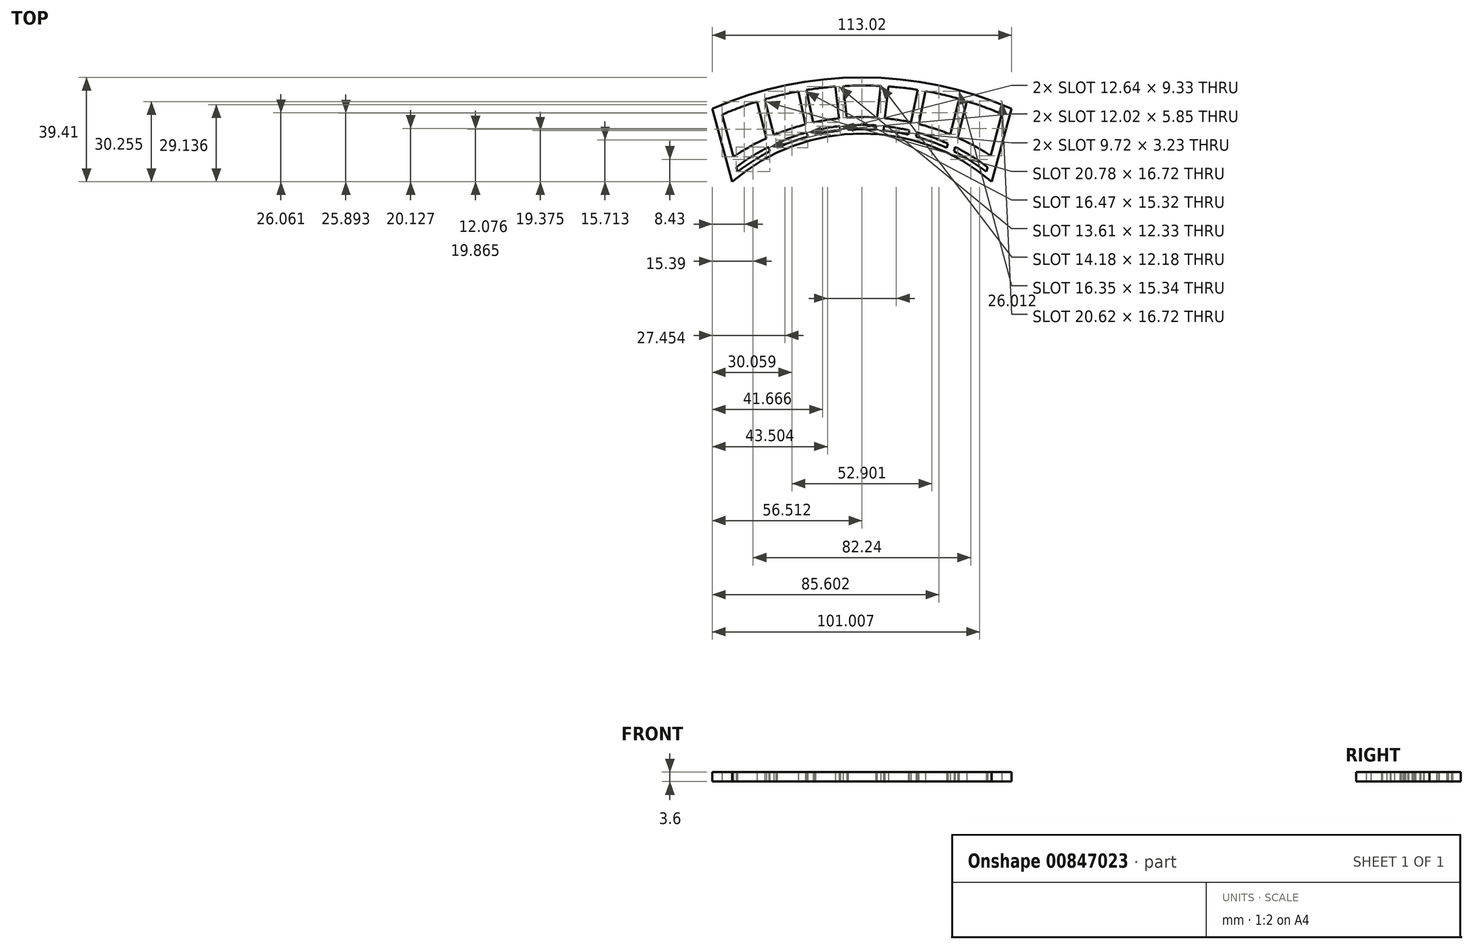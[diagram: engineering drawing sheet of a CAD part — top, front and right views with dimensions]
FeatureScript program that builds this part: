
annotation { "Feature Type Name" : "Feature", "Feature Type Description" : "" }
export const myFeature = defineFeature(function(context is Context, id is Id, definition is map)
    precondition{}
    {
        {
            var Q0;
            Q0=qCreatedBy(makeId("Top.planeOp"),FACE);
            var sketch = newSketch(context, id + "F0", { "sketchPlane" : qUnion([Q0])});
            skArc(sketch, "E0", {"start": v(50, 0) * mm, "mid": v(0, 17.98) * mm, "end": v(-50, 0) * mm});
            skLineSegment(sketch, "E1", {"start": v(-49.07, -3.46) * mm, "end": v(-56.5, 24.14) * mm});
            skLineSegment(sketch, "E2.MirrorCS", {"start": v(49.07, -3.46) * mm, "end": v(56.5, 24.14) * mm});
            skPoint(sketch, "E3", {"position": v(0, 35.95) * mm});
            skPoint(sketch, "E3.positionSnap0", {"position": v(0, 17.98) * mm});
            skArc(sketch, "E4", {"start": v(56.5, 24.14) * mm, "mid": v(0, 35.95) * mm, "end": v(-56.5, 24.14) * mm});
            skLineSegment(sketch, "E5", {"start": v(-53.72, 25.32) * mm, "end": v(-46.52, -1.37) * mm});
            skLineSegment(sketch, "E6", {"start": v(-40.42, 30.04) * mm, "end": v(-34.4, 6.4) * mm});
            skLineSegment(sketch, "E7", {"start": v(-37.53, 30.87) * mm, "end": v(-31.64, 7.75) * mm});
            skLineSegment(sketch, "E8", {"start": v(-20.12, 11.99) * mm, "end": v(-24.6, 33.79) * mm});
            skLineSegment(sketch, "E9", {"start": v(-17.2, 12.73) * mm, "end": v(-21.65, 34.28) * mm});
            skLineSegment(sketch, "E10", {"start": v(-10.45, 35.56) * mm, "end": v(-7.96, 14.3) * mm});
            skLineSegment(sketch, "E11", {"start": v(-7.45, 35.75) * mm, "end": v(-4.97, 14.56) * mm});
            skLineSegment(sketch, "E12.MirrorCS", {"start": v(7.45, 35.75) * mm, "end": v(4.97, 14.56) * mm});
            skLineSegment(sketch, "E13.MirrorCS", {"start": v(10.45, 35.56) * mm, "end": v(7.96, 14.3) * mm});
            skLineSegment(sketch, "E14.MirrorCS", {"start": v(17.2, 12.73) * mm, "end": v(21.65, 34.28) * mm});
            skLineSegment(sketch, "E15.MirrorCS", {"start": v(20.12, 11.99) * mm, "end": v(24.6, 33.79) * mm});
            skLineSegment(sketch, "E16.MirrorCS", {"start": v(37.53, 30.87) * mm, "end": v(31.64, 7.75) * mm});
            skLineSegment(sketch, "E17.MirrorCS", {"start": v(40.42, 30.04) * mm, "end": v(34.4, 6.4) * mm});
            skLineSegment(sketch, "E18.MirrorCS", {"start": v(53.72, 25.32) * mm, "end": v(46.52, -1.37) * mm});
            skArc(sketch, "E19", {"start": v(55.64, 20.9) * mm, "mid": v(0, 32.89) * mm, "end": v(-55.57, 20.66) * mm});
            skPoint(sketch, "E19.startSnap0", {"position": v(-35, 20.9) * mm});
            skArc(sketch, "E20", {"start": v(51.23, 4.55) * mm, "mid": v(0, 20.9) * mm, "end": v(-51.13, 4.18) * mm});
            skPoint(sketch, "E20.midSnap0", {"position": v(35, 20.9) * mm});
            skPoint(sketch, "E20.midSnap1", {"position": v(0, 32.89) * mm});
            skArc(sketch, "E21.0", {"start": v(49.53, -1.75) * mm, "mid": v(0, 16.33) * mm, "end": v(-49.53, -1.75) * mm});
            skArc(sketch, "E22.0", {"start": v(49.07, -3.46) * mm, "mid": v(0, 14.73) * mm, "end": v(-49.07, -3.46) * mm});
            skPoint(sketch, "E23.orphan", {"position": v(-47.44, 2.03) * mm});
            skPoint(sketch, "E24.orphan", {"position": v(-35.22, 9.64) * mm});
            skPoint(sketch, "E25.orphan", {"position": v(-32.46, 10.95) * mm});
            skPoint(sketch, "E26.orphan", {"position": v(-20.78, 15.18) * mm});
            skPoint(sketch, "E27.orphan", {"position": v(-17.87, 15.92) * mm});
            skPoint(sketch, "E28.orphan", {"position": v(-8.34, 17.53) * mm});
            skPoint(sketch, "E29.orphan", {"position": v(-5.35, 17.8) * mm});
            skPoint(sketch, "E30.orphan", {"position": v(5.35, 17.8) * mm});
            skPoint(sketch, "E31.orphan", {"position": v(8.34, 17.53) * mm});
            skPoint(sketch, "E32.orphan", {"position": v(17.87, 15.92) * mm});
            skPoint(sketch, "E33.orphan", {"position": v(20.78, 15.18) * mm});
            skPoint(sketch, "E34.orphan", {"position": v(32.46, 10.95) * mm});
            skPoint(sketch, "E35.orphan", {"position": v(35.22, 9.64) * mm});
            skPoint(sketch, "E36.orphan", {"position": v(47.44, 2.03) * mm});
            skPoint(sketch, "E37.orphan", {"position": v(50, 0) * mm});
            skSolve(sketch);
        }
        {
            var Q0;
            {var subQ0=sQuery(id+"F0.wireOp",EDGE,"E4");var subQ1=sQuery(id+"F0.wireOp",EDGE,"E1");var subQ2=makeQuery(id+"F0.imprint","INTERSECT",VERTEX,{"derivedFrom":[subQ1,subQ0]});Q0=makeQuery(id+"F0.imprint","IMPRINT",FACE,{"disambiguationData":[TD([[makeQuery(id+"F0.imprint","IMPRINT",EDGE,{"disambiguationData":[TD([[subQ2,1.0]])],"derivedFrom":subQ1}),-1.0]])]});}
            var Q1;
            {var subQ0=sQuery(id+"F0.wireOp",EDGE,"E5");var subQ1=sQuery(id+"F0.wireOp",EDGE,"E4");var subQ2=makeQuery(id+"F0.imprint","INTERSECT",VERTEX,{"derivedFrom":[subQ1,subQ0]});Q1=makeQuery(id+"F0.imprint","IMPRINT",FACE,{"disambiguationData":[TD([[makeQuery(id+"F0.imprint","IMPRINT",EDGE,{"disambiguationData":[TD([[subQ2,1.0]])],"derivedFrom":subQ1}),1.0]])]});}
            var Q2;
            {var subQ0=sQuery(id+"F0.wireOp",EDGE,"E6");var subQ1=sQuery(id+"F0.wireOp",EDGE,"E4");var subQ2=makeQuery(id+"F0.imprint","INTERSECT",VERTEX,{"derivedFrom":[subQ1,subQ0]});Q2=makeQuery(id+"F0.imprint","IMPRINT",FACE,{"disambiguationData":[TD([[makeQuery(id+"F0.imprint","IMPRINT",EDGE,{"disambiguationData":[TD([[subQ2,1.0]])],"derivedFrom":subQ1}),1.0]])]});}
            var Q3;
            {var subQ0=sQuery(id+"F0.wireOp",EDGE,"E7");var subQ1=sQuery(id+"F0.wireOp",EDGE,"E4");var subQ2=makeQuery(id+"F0.imprint","INTERSECT",VERTEX,{"derivedFrom":[subQ1,subQ0]});Q3=makeQuery(id+"F0.imprint","IMPRINT",FACE,{"disambiguationData":[TD([[makeQuery(id+"F0.imprint","IMPRINT",EDGE,{"disambiguationData":[TD([[subQ2,1.0]])],"derivedFrom":subQ1}),1.0]])]});}
            var Q4;
            {var subQ0=sQuery(id+"F0.wireOp",EDGE,"E8");var subQ1=sQuery(id+"F0.wireOp",EDGE,"E4");var subQ2=makeQuery(id+"F0.imprint","INTERSECT",VERTEX,{"derivedFrom":[subQ1,subQ0]});Q4=makeQuery(id+"F0.imprint","IMPRINT",FACE,{"disambiguationData":[TD([[makeQuery(id+"F0.imprint","IMPRINT",EDGE,{"disambiguationData":[TD([[subQ2,1.0]])],"derivedFrom":subQ1}),1.0]])]});}
            var Q5;
            {var subQ0=sQuery(id+"F0.wireOp",EDGE,"E9");var subQ1=sQuery(id+"F0.wireOp",EDGE,"E4");var subQ2=makeQuery(id+"F0.imprint","INTERSECT",VERTEX,{"derivedFrom":[subQ1,subQ0]});Q5=makeQuery(id+"F0.imprint","IMPRINT",FACE,{"disambiguationData":[TD([[makeQuery(id+"F0.imprint","IMPRINT",EDGE,{"disambiguationData":[TD([[subQ2,1.0]])],"derivedFrom":subQ1}),1.0]])]});}
            var Q6;
            {var subQ0=sQuery(id+"F0.wireOp",EDGE,"E10");var subQ1=sQuery(id+"F0.wireOp",EDGE,"E4");var subQ2=makeQuery(id+"F0.imprint","INTERSECT",VERTEX,{"derivedFrom":[subQ1,subQ0]});Q6=makeQuery(id+"F0.imprint","IMPRINT",FACE,{"disambiguationData":[TD([[makeQuery(id+"F0.imprint","IMPRINT",EDGE,{"disambiguationData":[TD([[subQ2,1.0]])],"derivedFrom":subQ1}),1.0]])]});}
            var Q7;
            {var subQ0=sQuery(id+"F0.wireOp",EDGE,"E11");var subQ1=sQuery(id+"F0.wireOp",EDGE,"E4");var subQ2=makeQuery(id+"F0.imprint","INTERSECT",VERTEX,{"derivedFrom":[subQ1,subQ0]});Q7=makeQuery(id+"F0.imprint","IMPRINT",FACE,{"disambiguationData":[TD([[makeQuery(id+"F0.imprint","IMPRINT",EDGE,{"disambiguationData":[TD([[subQ2,1.0]])],"derivedFrom":subQ1}),1.0]])]});}
            var Q8;
            {var subQ0=sQuery(id+"F0.wireOp",EDGE,"E12.MirrorCS");var subQ1=sQuery(id+"F0.wireOp",EDGE,"E4");var subQ2=makeQuery(id+"F0.imprint","INTERSECT",VERTEX,{"derivedFrom":[subQ1,subQ0]});Q8=makeQuery(id+"F0.imprint","IMPRINT",FACE,{"disambiguationData":[TD([[makeQuery(id+"F0.imprint","IMPRINT",EDGE,{"disambiguationData":[TD([[subQ2,1.0]])],"derivedFrom":subQ1}),1.0]])]});}
            var Q9;
            {var subQ0=sQuery(id+"F0.wireOp",EDGE,"E13.MirrorCS");var subQ1=sQuery(id+"F0.wireOp",EDGE,"E4");var subQ2=makeQuery(id+"F0.imprint","INTERSECT",VERTEX,{"derivedFrom":[subQ1,subQ0]});Q9=makeQuery(id+"F0.imprint","IMPRINT",FACE,{"disambiguationData":[TD([[makeQuery(id+"F0.imprint","IMPRINT",EDGE,{"disambiguationData":[TD([[subQ2,1.0]])],"derivedFrom":subQ1}),1.0]])]});}
            var Q10;
            {var subQ0=sQuery(id+"F0.wireOp",EDGE,"E14.MirrorCS");var subQ1=sQuery(id+"F0.wireOp",EDGE,"E4");var subQ2=makeQuery(id+"F0.imprint","INTERSECT",VERTEX,{"derivedFrom":[subQ1,subQ0]});Q10=makeQuery(id+"F0.imprint","IMPRINT",FACE,{"disambiguationData":[TD([[makeQuery(id+"F0.imprint","IMPRINT",EDGE,{"disambiguationData":[TD([[subQ2,1.0]])],"derivedFrom":subQ1}),1.0]])]});}
            var Q11;
            {var subQ0=sQuery(id+"F0.wireOp",EDGE,"E15.MirrorCS");var subQ1=sQuery(id+"F0.wireOp",EDGE,"E4");var subQ2=makeQuery(id+"F0.imprint","INTERSECT",VERTEX,{"derivedFrom":[subQ1,subQ0]});Q11=makeQuery(id+"F0.imprint","IMPRINT",FACE,{"disambiguationData":[TD([[makeQuery(id+"F0.imprint","IMPRINT",EDGE,{"disambiguationData":[TD([[subQ2,1.0]])],"derivedFrom":subQ1}),1.0]])]});}
            var Q12;
            {var subQ0=sQuery(id+"F0.wireOp",EDGE,"E16.MirrorCS");var subQ1=sQuery(id+"F0.wireOp",EDGE,"E4");var subQ2=makeQuery(id+"F0.imprint","INTERSECT",VERTEX,{"derivedFrom":[subQ1,subQ0]});Q12=makeQuery(id+"F0.imprint","IMPRINT",FACE,{"disambiguationData":[TD([[makeQuery(id+"F0.imprint","IMPRINT",EDGE,{"disambiguationData":[TD([[subQ2,1.0]])],"derivedFrom":subQ1}),1.0]])]});}
            var Q13;
            {var subQ0=sQuery(id+"F0.wireOp",EDGE,"E17.MirrorCS");var subQ1=sQuery(id+"F0.wireOp",EDGE,"E4");var subQ2=makeQuery(id+"F0.imprint","INTERSECT",VERTEX,{"derivedFrom":[subQ1,subQ0]});Q13=makeQuery(id+"F0.imprint","IMPRINT",FACE,{"disambiguationData":[TD([[makeQuery(id+"F0.imprint","IMPRINT",EDGE,{"disambiguationData":[TD([[subQ2,1.0]])],"derivedFrom":subQ1}),1.0]])]});}
            var Q14;
            {var subQ0=sQuery(id+"F0.wireOp",EDGE,"E4");var subQ1=sQuery(id+"F0.wireOp",EDGE,"E2.MirrorCS");var subQ2=makeQuery(id+"F0.imprint","INTERSECT",VERTEX,{"derivedFrom":[subQ1,subQ0]});Q14=makeQuery(id+"F0.imprint","IMPRINT",FACE,{"disambiguationData":[TD([[makeQuery(id+"F0.imprint","IMPRINT",EDGE,{"disambiguationData":[TD([[subQ2,1.0]])],"derivedFrom":subQ1}),1.0]])]});}
            var Q15;
            {var subQ0=sQuery(id+"F0.wireOp",EDGE,"E22.0");var subQ1=sQuery(id+"F0.wireOp",EDGE,"E1");var subQ2=makeQuery(id+"F0.imprint","INTERSECT",VERTEX,{"derivedFrom":[subQ1,subQ0]});Q15=makeQuery(id+"F0.imprint","IMPRINT",FACE,{"disambiguationData":[TD([[makeQuery(id+"F0.imprint","IMPRINT",EDGE,{"disambiguationData":[TD([[subQ2,-1.0]])],"derivedFrom":subQ1}),-1.0]])]});}
            var Q16;
            {var subQ0=sQuery(id+"F0.wireOp",EDGE,"E22.0");var subQ1=sQuery(id+"F0.wireOp",EDGE,"E5");var subQ2=makeQuery(id+"F0.imprint","INTERSECT",VERTEX,{"derivedFrom":[subQ1,subQ0]});Q16=makeQuery(id+"F0.imprint","IMPRINT",FACE,{"disambiguationData":[TD([[makeQuery(id+"F0.imprint","IMPRINT",EDGE,{"disambiguationData":[TD([[subQ2,1.0]])],"derivedFrom":subQ1}),1.0]])]});}
            var Q17;
            {var subQ0=sQuery(id+"F0.wireOp",EDGE,"E22.0");var subQ1=sQuery(id+"F0.wireOp",EDGE,"E6");var subQ2=makeQuery(id+"F0.imprint","INTERSECT",VERTEX,{"derivedFrom":[subQ1,subQ0]});Q17=makeQuery(id+"F0.imprint","IMPRINT",FACE,{"disambiguationData":[TD([[makeQuery(id+"F0.imprint","IMPRINT",EDGE,{"disambiguationData":[TD([[subQ2,1.0]])],"derivedFrom":subQ1}),1.0]])]});}
            var Q18;
            {var subQ0=sQuery(id+"F0.wireOp",EDGE,"E22.0");var subQ1=sQuery(id+"F0.wireOp",EDGE,"E7");var subQ2=makeQuery(id+"F0.imprint","INTERSECT",VERTEX,{"derivedFrom":[subQ1,subQ0]});Q18=makeQuery(id+"F0.imprint","IMPRINT",FACE,{"disambiguationData":[TD([[makeQuery(id+"F0.imprint","IMPRINT",EDGE,{"disambiguationData":[TD([[subQ2,1.0]])],"derivedFrom":subQ1}),1.0]])]});}
            var Q19;
            {var subQ0=sQuery(id+"F0.wireOp",EDGE,"E22.0");var subQ1=sQuery(id+"F0.wireOp",EDGE,"E8");var subQ2=makeQuery(id+"F0.imprint","INTERSECT",VERTEX,{"derivedFrom":[subQ1,subQ0]});Q19=makeQuery(id+"F0.imprint","IMPRINT",FACE,{"disambiguationData":[TD([[makeQuery(id+"F0.imprint","IMPRINT",EDGE,{"disambiguationData":[TD([[subQ2,-1.0]])],"derivedFrom":subQ1}),-1.0]])]});}
            var Q20;
            {var subQ0=sQuery(id+"F0.wireOp",EDGE,"E22.0");var subQ1=sQuery(id+"F0.wireOp",EDGE,"E9");var subQ2=makeQuery(id+"F0.imprint","INTERSECT",VERTEX,{"derivedFrom":[subQ1,subQ0]});Q20=makeQuery(id+"F0.imprint","IMPRINT",FACE,{"disambiguationData":[TD([[makeQuery(id+"F0.imprint","IMPRINT",EDGE,{"disambiguationData":[TD([[subQ2,-1.0]])],"derivedFrom":subQ1}),-1.0]])]});}
            var Q21;
            {var subQ0=sQuery(id+"F0.wireOp",EDGE,"E22.0");var subQ1=sQuery(id+"F0.wireOp",EDGE,"E10");var subQ2=makeQuery(id+"F0.imprint","INTERSECT",VERTEX,{"derivedFrom":[subQ1,subQ0]});Q21=makeQuery(id+"F0.imprint","IMPRINT",FACE,{"disambiguationData":[TD([[makeQuery(id+"F0.imprint","IMPRINT",EDGE,{"disambiguationData":[TD([[subQ2,1.0]])],"derivedFrom":subQ1}),1.0]])]});}
            var Q22;
            {var subQ0=sQuery(id+"F0.wireOp",EDGE,"E22.0");var subQ1=sQuery(id+"F0.wireOp",EDGE,"E11");var subQ2=makeQuery(id+"F0.imprint","INTERSECT",VERTEX,{"derivedFrom":[subQ1,subQ0]});Q22=makeQuery(id+"F0.imprint","IMPRINT",FACE,{"disambiguationData":[TD([[makeQuery(id+"F0.imprint","IMPRINT",EDGE,{"disambiguationData":[TD([[subQ2,1.0]])],"derivedFrom":subQ1}),1.0]])]});}
            var Q23;
            {var subQ0=sQuery(id+"F0.wireOp",EDGE,"E22.0");var subQ1=sQuery(id+"F0.wireOp",EDGE,"E12.MirrorCS");var subQ2=makeQuery(id+"F0.imprint","INTERSECT",VERTEX,{"derivedFrom":[subQ1,subQ0]});Q23=makeQuery(id+"F0.imprint","IMPRINT",FACE,{"disambiguationData":[TD([[makeQuery(id+"F0.imprint","IMPRINT",EDGE,{"disambiguationData":[TD([[subQ2,1.0]])],"derivedFrom":subQ1}),1.0]])]});}
            var Q24;
            {var subQ0=sQuery(id+"F0.wireOp",EDGE,"E22.0");var subQ1=sQuery(id+"F0.wireOp",EDGE,"E13.MirrorCS");var subQ2=makeQuery(id+"F0.imprint","INTERSECT",VERTEX,{"derivedFrom":[subQ1,subQ0]});Q24=makeQuery(id+"F0.imprint","IMPRINT",FACE,{"disambiguationData":[TD([[makeQuery(id+"F0.imprint","IMPRINT",EDGE,{"disambiguationData":[TD([[subQ2,1.0]])],"derivedFrom":subQ1}),1.0]])]});}
            var Q25;
            {var subQ0=sQuery(id+"F0.wireOp",EDGE,"E22.0");var subQ1=sQuery(id+"F0.wireOp",EDGE,"E14.MirrorCS");var subQ2=makeQuery(id+"F0.imprint","INTERSECT",VERTEX,{"derivedFrom":[subQ1,subQ0]});Q25=makeQuery(id+"F0.imprint","IMPRINT",FACE,{"disambiguationData":[TD([[makeQuery(id+"F0.imprint","IMPRINT",EDGE,{"disambiguationData":[TD([[subQ2,-1.0]])],"derivedFrom":subQ1}),-1.0]])]});}
            var Q26;
            {var subQ0=sQuery(id+"F0.wireOp",EDGE,"E22.0");var subQ1=sQuery(id+"F0.wireOp",EDGE,"E15.MirrorCS");var subQ2=makeQuery(id+"F0.imprint","INTERSECT",VERTEX,{"derivedFrom":[subQ1,subQ0]});Q26=makeQuery(id+"F0.imprint","IMPRINT",FACE,{"disambiguationData":[TD([[makeQuery(id+"F0.imprint","IMPRINT",EDGE,{"disambiguationData":[TD([[subQ2,-1.0]])],"derivedFrom":subQ1}),-1.0]])]});}
            var Q27;
            {var subQ0=sQuery(id+"F0.wireOp",EDGE,"E22.0");var subQ1=sQuery(id+"F0.wireOp",EDGE,"E16.MirrorCS");var subQ2=makeQuery(id+"F0.imprint","INTERSECT",VERTEX,{"derivedFrom":[subQ1,subQ0]});Q27=makeQuery(id+"F0.imprint","IMPRINT",FACE,{"disambiguationData":[TD([[makeQuery(id+"F0.imprint","IMPRINT",EDGE,{"disambiguationData":[TD([[subQ2,1.0]])],"derivedFrom":subQ1}),1.0]])]});}
            var Q28;
            {var subQ0=sQuery(id+"F0.wireOp",EDGE,"E22.0");var subQ1=sQuery(id+"F0.wireOp",EDGE,"E17.MirrorCS");var subQ2=makeQuery(id+"F0.imprint","INTERSECT",VERTEX,{"derivedFrom":[subQ1,subQ0]});Q28=makeQuery(id+"F0.imprint","IMPRINT",FACE,{"disambiguationData":[TD([[makeQuery(id+"F0.imprint","IMPRINT",EDGE,{"disambiguationData":[TD([[subQ2,1.0]])],"derivedFrom":subQ1}),1.0]])]});}
            var Q29;
            {var subQ0=sQuery(id+"F0.wireOp",EDGE,"E22.0");var subQ1=sQuery(id+"F0.wireOp",EDGE,"E2.MirrorCS");var subQ2=makeQuery(id+"F0.imprint","INTERSECT",VERTEX,{"derivedFrom":[subQ1,subQ0]});Q29=makeQuery(id+"F0.imprint","IMPRINT",FACE,{"disambiguationData":[TD([[makeQuery(id+"F0.imprint","IMPRINT",EDGE,{"disambiguationData":[TD([[subQ2,-1.0]])],"derivedFrom":subQ1}),1.0]])]});}
            var Q30;
            {var subQ0=sQuery(id+"F0.wireOp",EDGE,"E1");var subQ1=sQuery(id+"F0.wireOp",EDGE,"E0");var subQ2=makeQuery(id+"F0.imprint","INTERSECT",VERTEX,{"derivedFrom":[subQ1,subQ0]});Q30=makeQuery(id+"F0.imprint","IMPRINT",FACE,{"disambiguationData":[TD([[makeQuery(id+"F0.imprint","IMPRINT",EDGE,{"disambiguationData":[TD([[subQ2,1.0]])],"derivedFrom":subQ1}),1.0]])]});}
            var Q31;
            {var subQ0=sQuery(id+"F0.wireOp",EDGE,"E1");var subQ1=sQuery(id+"F0.wireOp",EDGE,"E0");var subQ2=makeQuery(id+"F0.imprint","INTERSECT",VERTEX,{"derivedFrom":[subQ1,subQ0]});Q31=makeQuery(id+"F0.imprint","IMPRINT",FACE,{"disambiguationData":[TD([[makeQuery(id+"F0.imprint","IMPRINT",EDGE,{"disambiguationData":[TD([[subQ2,1.0]])],"derivedFrom":subQ1}),-1.0]])]});}
            var Q32;
            {var subQ0=sQuery(id+"F0.wireOp",EDGE,"E19");var subQ1=sQuery(id+"F0.wireOp",EDGE,"E1");var subQ2=makeQuery(id+"F0.imprint","INTERSECT",VERTEX,{"derivedFrom":[subQ1,subQ0]});Q32=makeQuery(id+"F0.imprint","IMPRINT",FACE,{"disambiguationData":[TD([[makeQuery(id+"F0.imprint","IMPRINT",EDGE,{"disambiguationData":[TD([[subQ2,1.0]])],"derivedFrom":subQ1}),-1.0]])]});}
            var Q33;
            {var subQ0=sQuery(id+"F0.wireOp",EDGE,"E6");var subQ1=sQuery(id+"F0.wireOp",EDGE,"E0");var subQ2=makeQuery(id+"F0.imprint","INTERSECT",VERTEX,{"derivedFrom":[subQ1,subQ0]});Q33=makeQuery(id+"F0.imprint","IMPRINT",FACE,{"disambiguationData":[TD([[makeQuery(id+"F0.imprint","IMPRINT",EDGE,{"disambiguationData":[TD([[subQ2,-1.0]])],"derivedFrom":subQ1}),-1.0]])]});}
            var Q34;
            {var subQ0=sQuery(id+"F0.wireOp",EDGE,"E7");var subQ1=sQuery(id+"F0.wireOp",EDGE,"E0");var subQ2=makeQuery(id+"F0.imprint","INTERSECT",VERTEX,{"derivedFrom":[subQ1,subQ0]});Q34=makeQuery(id+"F0.imprint","IMPRINT",FACE,{"disambiguationData":[TD([[makeQuery(id+"F0.imprint","IMPRINT",EDGE,{"disambiguationData":[TD([[subQ2,-1.0]])],"derivedFrom":subQ1}),-1.0]])]});}
            var Q35;
            {var subQ0=sQuery(id+"F0.wireOp",EDGE,"E19");var subQ1=sQuery(id+"F0.wireOp",EDGE,"E6");var subQ2=makeQuery(id+"F0.imprint","INTERSECT",VERTEX,{"derivedFrom":[subQ1,subQ0]});Q35=makeQuery(id+"F0.imprint","IMPRINT",FACE,{"disambiguationData":[TD([[makeQuery(id+"F0.imprint","IMPRINT",EDGE,{"disambiguationData":[TD([[subQ2,-1.0]])],"derivedFrom":subQ1}),1.0]])]});}
            var Q36;
            {var subQ0=sQuery(id+"F0.wireOp",EDGE,"E8");var subQ1=sQuery(id+"F0.wireOp",EDGE,"E0");var subQ2=makeQuery(id+"F0.imprint","INTERSECT",VERTEX,{"derivedFrom":[subQ1,subQ0]});Q36=makeQuery(id+"F0.imprint","IMPRINT",FACE,{"disambiguationData":[TD([[makeQuery(id+"F0.imprint","IMPRINT",EDGE,{"disambiguationData":[TD([[subQ2,-1.0]])],"derivedFrom":subQ1}),-1.0]])]});}
            var Q37;
            {var subQ0=sQuery(id+"F0.wireOp",EDGE,"E20");var subQ1=sQuery(id+"F0.wireOp",EDGE,"E8");var subQ2=makeQuery(id+"F0.imprint","INTERSECT",VERTEX,{"derivedFrom":[subQ1,subQ0]});Q37=makeQuery(id+"F0.imprint","IMPRINT",FACE,{"disambiguationData":[TD([[makeQuery(id+"F0.imprint","IMPRINT",EDGE,{"disambiguationData":[TD([[subQ2,-1.0]])],"derivedFrom":subQ1}),-1.0]])]});}
            var Q38;
            {var subQ0=sQuery(id+"F0.wireOp",EDGE,"E9");var subQ1=sQuery(id+"F0.wireOp",EDGE,"E0");var subQ2=makeQuery(id+"F0.imprint","INTERSECT",VERTEX,{"derivedFrom":[subQ1,subQ0]});Q38=makeQuery(id+"F0.imprint","IMPRINT",FACE,{"disambiguationData":[TD([[makeQuery(id+"F0.imprint","IMPRINT",EDGE,{"disambiguationData":[TD([[subQ2,-1.0]])],"derivedFrom":subQ1}),-1.0]])]});}
            var Q39;
            {var subQ0=sQuery(id+"F0.wireOp",EDGE,"E10");var subQ1=sQuery(id+"F0.wireOp",EDGE,"E0");var subQ2=makeQuery(id+"F0.imprint","INTERSECT",VERTEX,{"derivedFrom":[subQ1,subQ0]});Q39=makeQuery(id+"F0.imprint","IMPRINT",FACE,{"disambiguationData":[TD([[makeQuery(id+"F0.imprint","IMPRINT",EDGE,{"disambiguationData":[TD([[subQ2,-1.0]])],"derivedFrom":subQ1}),-1.0]])]});}
            var Q40;
            {var subQ0=sQuery(id+"F0.wireOp",EDGE,"E19");var subQ1=sQuery(id+"F0.wireOp",EDGE,"E10");var subQ2=makeQuery(id+"F0.imprint","INTERSECT",VERTEX,{"derivedFrom":[subQ1,subQ0]});Q40=makeQuery(id+"F0.imprint","IMPRINT",FACE,{"disambiguationData":[TD([[makeQuery(id+"F0.imprint","IMPRINT",EDGE,{"disambiguationData":[TD([[subQ2,-1.0]])],"derivedFrom":subQ1}),1.0]])]});}
            var Q41;
            {var subQ0=sQuery(id+"F0.wireOp",EDGE,"E11");var subQ1=sQuery(id+"F0.wireOp",EDGE,"E0");var subQ2=makeQuery(id+"F0.imprint","INTERSECT",VERTEX,{"derivedFrom":[subQ1,subQ0]});Q41=makeQuery(id+"F0.imprint","IMPRINT",FACE,{"disambiguationData":[TD([[makeQuery(id+"F0.imprint","IMPRINT",EDGE,{"disambiguationData":[TD([[subQ2,-1.0]])],"derivedFrom":subQ1}),-1.0]])]});}
            var Q42;
            {var subQ0=sQuery(id+"F0.wireOp",EDGE,"E20");var subQ1=sQuery(id+"F0.wireOp",EDGE,"E14.MirrorCS");var subQ2=makeQuery(id+"F0.imprint","INTERSECT",VERTEX,{"derivedFrom":[subQ1,subQ0]});Q42=makeQuery(id+"F0.imprint","IMPRINT",FACE,{"disambiguationData":[TD([[makeQuery(id+"F0.imprint","IMPRINT",EDGE,{"disambiguationData":[TD([[subQ2,-1.0]])],"derivedFrom":subQ1}),-1.0]])]});}
            var Q43;
            {var subQ0=sQuery(id+"F0.wireOp",EDGE,"E7");var subQ1=sQuery(id+"F0.wireOp",EDGE,"E0");var subQ2=makeQuery(id+"F0.imprint","INTERSECT",VERTEX,{"derivedFrom":[subQ1,subQ0]});Q43=makeQuery(id+"F0.imprint","IMPRINT",FACE,{"disambiguationData":[TD([[makeQuery(id+"F0.imprint","IMPRINT",EDGE,{"disambiguationData":[TD([[subQ2,-1.0]])],"derivedFrom":subQ1}),1.0]])]});}
            var Q44;
            {var subQ0=sQuery(id+"F0.wireOp",EDGE,"E9");var subQ1=sQuery(id+"F0.wireOp",EDGE,"E0");var subQ2=makeQuery(id+"F0.imprint","INTERSECT",VERTEX,{"derivedFrom":[subQ1,subQ0]});Q44=makeQuery(id+"F0.imprint","IMPRINT",FACE,{"disambiguationData":[TD([[makeQuery(id+"F0.imprint","IMPRINT",EDGE,{"disambiguationData":[TD([[subQ2,-1.0]])],"derivedFrom":subQ1}),1.0]])]});}
            var Q45;
            {var subQ0=sQuery(id+"F0.wireOp",EDGE,"E11");var subQ1=sQuery(id+"F0.wireOp",EDGE,"E0");var subQ2=makeQuery(id+"F0.imprint","INTERSECT",VERTEX,{"derivedFrom":[subQ1,subQ0]});Q45=makeQuery(id+"F0.imprint","IMPRINT",FACE,{"disambiguationData":[TD([[makeQuery(id+"F0.imprint","IMPRINT",EDGE,{"disambiguationData":[TD([[subQ2,-1.0]])],"derivedFrom":subQ1}),1.0]])]});}
            var Q46;
            {var subQ0=sQuery(id+"F0.wireOp",EDGE,"E19");var subQ1=sQuery(id+"F0.wireOp",EDGE,"E2.MirrorCS");var subQ2=makeQuery(id+"F0.imprint","INTERSECT",VERTEX,{"derivedFrom":[subQ1,subQ0]});Q46=makeQuery(id+"F0.imprint","IMPRINT",FACE,{"disambiguationData":[TD([[makeQuery(id+"F0.imprint","IMPRINT",EDGE,{"disambiguationData":[TD([[subQ2,1.0]])],"derivedFrom":subQ1}),1.0]])]});}
            var Q47;
            {var subQ0=sQuery(id+"F0.wireOp",EDGE,"E19");var subQ1=sQuery(id+"F0.wireOp",EDGE,"E16.MirrorCS");var subQ2=makeQuery(id+"F0.imprint","INTERSECT",VERTEX,{"derivedFrom":[subQ1,subQ0]});Q47=makeQuery(id+"F0.imprint","IMPRINT",FACE,{"disambiguationData":[TD([[makeQuery(id+"F0.imprint","IMPRINT",EDGE,{"disambiguationData":[TD([[subQ2,-1.0]])],"derivedFrom":subQ1}),1.0]])]});}
            var Q48;
            {var subQ0=sQuery(id+"F0.wireOp",EDGE,"E2.MirrorCS");var subQ1=sQuery(id+"F0.wireOp",EDGE,"E0");var subQ2=makeQuery(id+"F0.imprint","INTERSECT",VERTEX,{"derivedFrom":[subQ1,subQ0]});Q48=makeQuery(id+"F0.imprint","IMPRINT",FACE,{"disambiguationData":[TD([[makeQuery(id+"F0.imprint","IMPRINT",EDGE,{"disambiguationData":[TD([[subQ2,-1.0]])],"derivedFrom":subQ1}),-1.0]])]});}
            var Q49;
            {var subQ0=sQuery(id+"F0.wireOp",EDGE,"E2.MirrorCS");var subQ1=sQuery(id+"F0.wireOp",EDGE,"E0");var subQ2=makeQuery(id+"F0.imprint","INTERSECT",VERTEX,{"derivedFrom":[subQ1,subQ0]});Q49=makeQuery(id+"F0.imprint","IMPRINT",FACE,{"disambiguationData":[TD([[makeQuery(id+"F0.imprint","IMPRINT",EDGE,{"disambiguationData":[TD([[subQ2,-1.0]])],"derivedFrom":subQ1}),1.0]])]});}
            var Q50;
            {var subQ0=sQuery(id+"F0.wireOp",EDGE,"E17.MirrorCS");var subQ1=sQuery(id+"F0.wireOp",EDGE,"E0");var subQ2=makeQuery(id+"F0.imprint","INTERSECT",VERTEX,{"derivedFrom":[subQ1,subQ0]});Q50=makeQuery(id+"F0.imprint","IMPRINT",FACE,{"disambiguationData":[TD([[makeQuery(id+"F0.imprint","IMPRINT",EDGE,{"disambiguationData":[TD([[subQ2,-1.0]])],"derivedFrom":subQ1}),-1.0]])]});}
            var Q51;
            {var subQ0=sQuery(id+"F0.wireOp",EDGE,"E17.MirrorCS");var subQ1=sQuery(id+"F0.wireOp",EDGE,"E0");var subQ2=makeQuery(id+"F0.imprint","INTERSECT",VERTEX,{"derivedFrom":[subQ1,subQ0]});Q51=makeQuery(id+"F0.imprint","IMPRINT",FACE,{"disambiguationData":[TD([[makeQuery(id+"F0.imprint","IMPRINT",EDGE,{"disambiguationData":[TD([[subQ2,-1.0]])],"derivedFrom":subQ1}),1.0]])]});}
            var Q52;
            {var subQ0=sQuery(id+"F0.wireOp",EDGE,"E15.MirrorCS");var subQ1=sQuery(id+"F0.wireOp",EDGE,"E0");var subQ2=makeQuery(id+"F0.imprint","INTERSECT",VERTEX,{"derivedFrom":[subQ1,subQ0]});Q52=makeQuery(id+"F0.imprint","IMPRINT",FACE,{"disambiguationData":[TD([[makeQuery(id+"F0.imprint","IMPRINT",EDGE,{"disambiguationData":[TD([[subQ2,-1.0]])],"derivedFrom":subQ1}),1.0]])]});}
            var Q53;
            {var subQ0=sQuery(id+"F0.wireOp",EDGE,"E15.MirrorCS");var subQ1=sQuery(id+"F0.wireOp",EDGE,"E0");var subQ2=makeQuery(id+"F0.imprint","INTERSECT",VERTEX,{"derivedFrom":[subQ1,subQ0]});Q53=makeQuery(id+"F0.imprint","IMPRINT",FACE,{"disambiguationData":[TD([[makeQuery(id+"F0.imprint","IMPRINT",EDGE,{"disambiguationData":[TD([[subQ2,-1.0]])],"derivedFrom":subQ1}),-1.0]])]});}
            var Q54;
            {var subQ0=sQuery(id+"F0.wireOp",EDGE,"E16.MirrorCS");var subQ1=sQuery(id+"F0.wireOp",EDGE,"E0");var subQ2=makeQuery(id+"F0.imprint","INTERSECT",VERTEX,{"derivedFrom":[subQ1,subQ0]});Q54=makeQuery(id+"F0.imprint","IMPRINT",FACE,{"disambiguationData":[TD([[makeQuery(id+"F0.imprint","IMPRINT",EDGE,{"disambiguationData":[TD([[subQ2,-1.0]])],"derivedFrom":subQ1}),-1.0]])]});}
            var Q55;
            {var subQ0=sQuery(id+"F0.wireOp",EDGE,"E18.MirrorCS");var subQ1=sQuery(id+"F0.wireOp",EDGE,"E0");var subQ2=makeQuery(id+"F0.imprint","INTERSECT",VERTEX,{"derivedFrom":[subQ1,subQ0]});Q55=makeQuery(id+"F0.imprint","IMPRINT",FACE,{"disambiguationData":[TD([[makeQuery(id+"F0.imprint","IMPRINT",EDGE,{"disambiguationData":[TD([[subQ2,-1.0]])],"derivedFrom":subQ1}),-1.0]])]});}
            var Q56;
            {var subQ0=sQuery(id+"F0.wireOp",EDGE,"E13.MirrorCS");var subQ1=sQuery(id+"F0.wireOp",EDGE,"E0");var subQ2=makeQuery(id+"F0.imprint","INTERSECT",VERTEX,{"derivedFrom":[subQ1,subQ0]});Q56=makeQuery(id+"F0.imprint","IMPRINT",FACE,{"disambiguationData":[TD([[makeQuery(id+"F0.imprint","IMPRINT",EDGE,{"disambiguationData":[TD([[subQ2,-1.0]])],"derivedFrom":subQ1}),-1.0]])]});}
            var Q57;
            {var subQ0=sQuery(id+"F0.wireOp",EDGE,"E19");var subQ1=sQuery(id+"F0.wireOp",EDGE,"E12.MirrorCS");var subQ2=makeQuery(id+"F0.imprint","INTERSECT",VERTEX,{"derivedFrom":[subQ1,subQ0]});Q57=makeQuery(id+"F0.imprint","IMPRINT",FACE,{"disambiguationData":[TD([[makeQuery(id+"F0.imprint","IMPRINT",EDGE,{"disambiguationData":[TD([[subQ2,-1.0]])],"derivedFrom":subQ1}),1.0]])]});}
            var Q58;
            {var subQ0=sQuery(id+"F0.wireOp",EDGE,"E13.MirrorCS");var subQ1=sQuery(id+"F0.wireOp",EDGE,"E0");var subQ2=makeQuery(id+"F0.imprint","INTERSECT",VERTEX,{"derivedFrom":[subQ1,subQ0]});Q58=makeQuery(id+"F0.imprint","IMPRINT",FACE,{"disambiguationData":[TD([[makeQuery(id+"F0.imprint","IMPRINT",EDGE,{"disambiguationData":[TD([[subQ2,-1.0]])],"derivedFrom":subQ1}),1.0]])]});}
            var Q59;
            {var subQ0=sQuery(id+"F0.wireOp",EDGE,"E14.MirrorCS");var subQ1=sQuery(id+"F0.wireOp",EDGE,"E0");var subQ2=makeQuery(id+"F0.imprint","INTERSECT",VERTEX,{"derivedFrom":[subQ1,subQ0]});Q59=makeQuery(id+"F0.imprint","IMPRINT",FACE,{"disambiguationData":[TD([[makeQuery(id+"F0.imprint","IMPRINT",EDGE,{"disambiguationData":[TD([[subQ2,-1.0]])],"derivedFrom":subQ1}),-1.0]])]});}
            var Q60;
            {var subQ0=sQuery(id+"F0.wireOp",EDGE,"E12.MirrorCS");var subQ1=sQuery(id+"F0.wireOp",EDGE,"E0");var subQ2=makeQuery(id+"F0.imprint","INTERSECT",VERTEX,{"derivedFrom":[subQ1,subQ0]});Q60=makeQuery(id+"F0.imprint","IMPRINT",FACE,{"disambiguationData":[TD([[makeQuery(id+"F0.imprint","IMPRINT",EDGE,{"disambiguationData":[TD([[subQ2,-1.0]])],"derivedFrom":subQ1}),-1.0]])]});}
            extrude(context, id + "F1", {"entities" : qUnion([Q0, Q1, Q2, Q3, Q4, Q5, Q6, Q7, Q8, Q9, Q10, Q11, Q12, Q13, Q14, Q15, Q16, Q17, Q18, Q19, Q20, Q21, Q22, Q23, Q24, Q25, Q26, Q27, Q28, Q29, Q30, Q31, Q32, Q33, Q34, Q35, Q36, Q37, Q38, Q39, Q40, Q41, Q42, Q43, Q44, Q45, Q46, Q47, Q48, Q49, Q50, Q51, Q52, Q53, Q54, Q55, Q56, Q57, Q58, Q59, Q60]), "depth" : 3.6 * mm, "offsetDistance" : 25 * mm});
        }
    });
